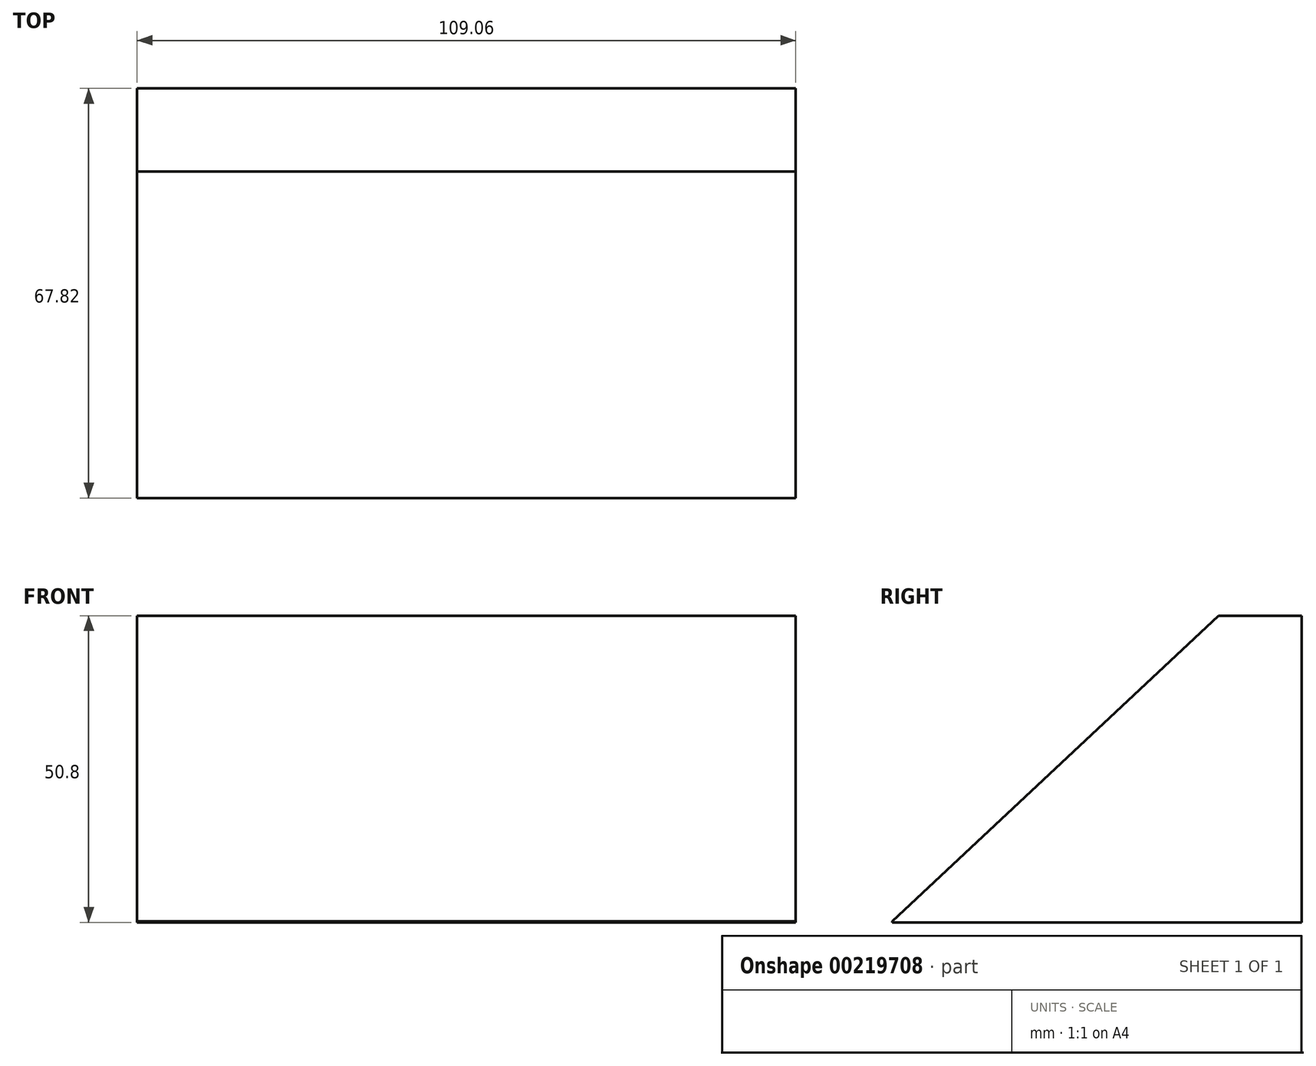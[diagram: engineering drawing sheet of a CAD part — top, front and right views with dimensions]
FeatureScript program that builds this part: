
annotation { "Feature Type Name" : "Feature", "Feature Type Description" : "" }
export const myFeature = defineFeature(function(context is Context, id is Id, definition is map)
    precondition{}
    {
        {
            var Q0;
            Q0=qCreatedBy(makeId("Top.planeOp"),FACE);
            var sketch = newSketch(context, id + "F0", { "sketchPlane" : qUnion([Q0])});
            skLineSegment(sketch, "E0.bottom", {"start": v(-55.54, 34.55) * mm, "end": v(53.52, 34.55) * mm});
            skLineSegment(sketch, "E0.top", {"start": v(-55.54, -33.27) * mm, "end": v(53.52, -33.27) * mm});
            skLineSegment(sketch, "E0.left", {"start": v(-55.54, 34.55) * mm, "end": v(-55.54, -33.27) * mm});
            skLineSegment(sketch, "E0.right", {"start": v(53.52, 34.55) * mm, "end": v(53.52, -33.27) * mm});
            skSolve(sketch);
        }
        {
            var Q0;
            Q0=makeQuery(id+"F0.imprint","IMPRINT",FACE,{"disambiguationData":[TD([[makeQuery(id+"F0.imprint","IMPRINT",EDGE,{"derivedFrom":sQuery(id+"F0.wireOp",EDGE,"E0.bottom")}),-1.0]])]});
            extrude(context, id + "F1", {"entities" : qUnion([Q0]), "depth" : 50.8 * mm});
        }
        {
            var Q0;
            Q0=qCreatedBy(makeId("Top.planeOp"),FACE);
            var sketch = newSketch(context, id + "F2", { "sketchPlane" : qUnion([Q0])});
            skLineSegment(sketch, "E1.bottom", {"start": v(59.94, 34.37) * mm, "end": v(54.62, 34.37) * mm});
            skLineSegment(sketch, "E1.top", {"start": v(59.94, -33.45) * mm, "end": v(54.62, -33.45) * mm});
            skLineSegment(sketch, "E1.left", {"start": v(59.94, 34.37) * mm, "end": v(59.94, -33.45) * mm});
            skLineSegment(sketch, "E1.right", {"start": v(54.62, 34.37) * mm, "end": v(54.62, -33.45) * mm});
            skSolve(sketch);
        }
        {
            var Q0;
            Q0=makeQuery(id+"F2.imprint","IMPRINT",FACE,{"disambiguationData":[TD([[makeQuery(id+"F2.imprint","IMPRINT",EDGE,{"derivedFrom":sQuery(id+"F2.wireOp",EDGE,"E1.bottom")}),1.0]])]});
            extrude(context, id + "F3", {"entities" : qUnion([Q0]), "depth" : 63.5 * mm});
        }
        {
            var Q0;
            Q0=makeQuery(id+"F1.opExtrude","SWEPT_FACE",FACE,{"disambiguationData":[OSD([sQuery(id+"F0.wireOp",EDGE,"E0.left")])]});
            var sketch = newSketch(context, id + "F4", { "sketchPlane" : qUnion([Q0])});
            skLineSegment(sketch, "E2.0", {"start": v(-34.55, 50.8) * mm, "end": v(33.27, 50.8) * mm});
            skLineSegment(sketch, "E3.0", {"start": v(33.27, 50.8) * mm, "end": v(33.27, 0) * mm});
            skLineSegment(sketch, "E4.0", {"start": v(33.45, 63.5) * mm, "end": v(33.45, 0) * mm});
            skLineSegment(sketch, "E5.0", {"start": v(-34.37, 63.5) * mm, "end": v(33.45, 63.5) * mm});
            skLineSegment(sketch, "E6", {"start": v(-34.37, 63.5) * mm, "end": v(33.45, 0) * mm});
            skSolve(sketch);
        }
        {
            var Q0;
            {var subQ2=sQuery(id+"F4.wireOp",EDGE,"E4.0");Q0=makeQuery(id+"F4.imprint","IMPRINT",FACE,{"disambiguationData":[TD([[makeQuery(id+"F4.imprint","IMPRINT",EDGE,{"derivedFrom":subQ2}),-1.0]])]});}
            var Q1;
            {var subQ0=sQuery(id+"F4.wireOp",EDGE,"E3.0");var subQ1=sQuery(id+"F4.wireOp",EDGE,"E2.0");var subQ2=makeQuery(id+"F4.imprint","INTERSECT",VERTEX,{"derivedFrom":[subQ1,subQ0]});Q1=makeQuery(id+"F4.imprint","IMPRINT",FACE,{"disambiguationData":[TD([[makeQuery(id+"F4.imprint","IMPRINT",EDGE,{"disambiguationData":[TD([[subQ2,1.0]])],"derivedFrom":subQ1}),-1.0]])]});}
            extrude(context, id + "F5", {"entities" : qUnion([Q0, Q1]), "operationType" : NewBodyOperationType.REMOVE, "oppositeDirection" : true, "depth" : 127 * mm});
        }
        {
            var Q0;
            Q0=makeQuery(id+"F3.opExtrude","SWEPT_FACE",FACE,{"disambiguationData":[OSD([sQuery(id+"F2.wireOp",EDGE,"E1.right")])]});
            var sketch = newSketch(context, id + "F6", { "sketchPlane" : qUnion([Q0])});
            skLineSegment(sketch, "E7", {"start": v(-34.37, 63.5) * mm, "end": v(33.45, 0) * mm});
            skSolve(sketch);
        }
        {
            var Q0;
            Q0=makeQuery(id+"F6.imprint","IMPRINT",FACE,{"disambiguationData":[TD([[makeQuery(id+"F6.imprint","IMPRINT",EDGE,{"derivedFrom":sQuery(id+"F6.wireOp",EDGE,"E7")}),1.0]])]});
            extrude(context, id + "F7", {"entities" : qUnion([Q0]), "operationType" : NewBodyOperationType.REMOVE, "oppositeDirection" : true, "depth" : 25.4 * mm});
        }
    });
